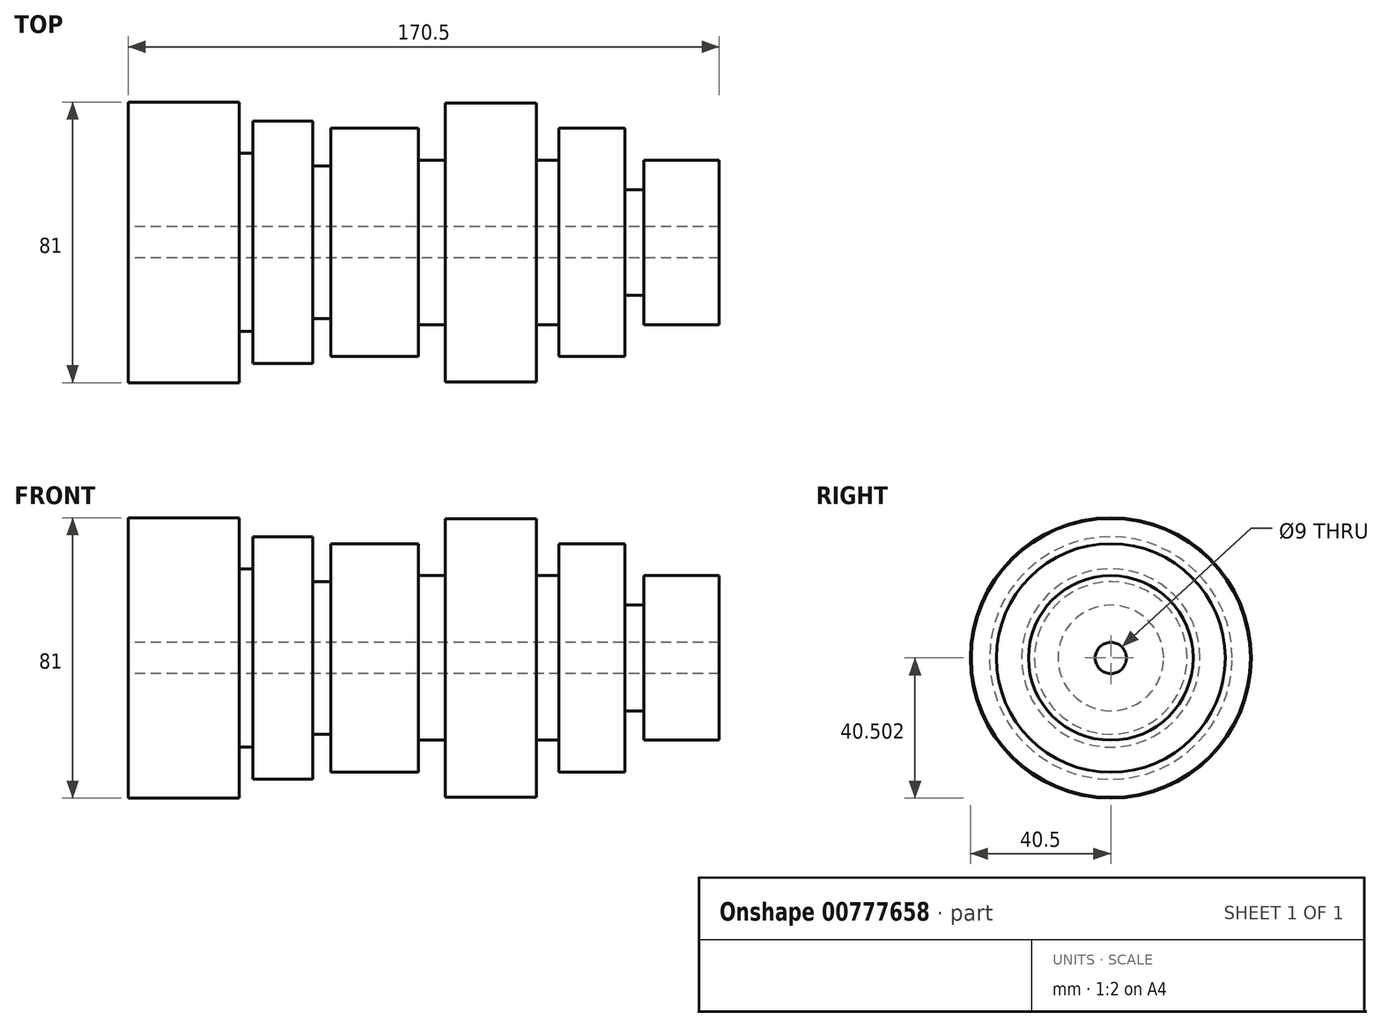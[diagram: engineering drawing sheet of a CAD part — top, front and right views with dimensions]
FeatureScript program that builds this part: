
annotation { "Feature Type Name" : "Feature", "Feature Type Description" : "" }
export const myFeature = defineFeature(function(context is Context, id is Id, definition is map)
    precondition{}
    {
        {
            var Q0;
            Q0=qCreatedBy(makeId("Front.planeOp"),FACE);
            var sketch = newSketch(context, id + "F0", { "sketchPlane" : qUnion([Q0])});
            skLineSegment(sketch, "E0", {"start": v(-87.13, -47.13) * mm, "end": v(83.37, -47.13) * mm});
            skLineSegment(sketch, "E1", {"start": v(-87.13, -47.13) * mm, "end": v(-87.13, -11.13) * mm});
            skLineSegment(sketch, "E2", {"start": v(-87.13, -11.13) * mm, "end": v(-55.13, -11.13) * mm});
            skLineSegment(sketch, "E3", {"start": v(-55.13, -11.13) * mm, "end": v(-55.13, -25.88) * mm});
            skLineSegment(sketch, "E4", {"start": v(-55.13, -25.88) * mm, "end": v(-51.13, -25.88) * mm});
            skLineSegment(sketch, "E5", {"start": v(-51.13, -25.88) * mm, "end": v(-51.13, -16.63) * mm});
            skLineSegment(sketch, "E6", {"start": v(-51.13, -16.63) * mm, "end": v(-33.88, -16.63) * mm});
            skLineSegment(sketch, "E7", {"start": v(-33.88, -16.63) * mm, "end": v(-33.88, -29.63) * mm});
            skLineSegment(sketch, "E8", {"start": v(83.37, -47.13) * mm, "end": v(83.37, -27.88) * mm});
            skLineSegment(sketch, "E9", {"start": v(83.37, -27.88) * mm, "end": v(61.63, -27.88) * mm});
            skLineSegment(sketch, "E10", {"start": v(61.63, -27.88) * mm, "end": v(61.63, -36.38) * mm});
            skLineSegment(sketch, "E11", {"start": v(61.63, -36.38) * mm, "end": v(56.13, -36.38) * mm});
            skLineSegment(sketch, "E12", {"start": v(56.13, -36.38) * mm, "end": v(56.13, -18.63) * mm});
            skLineSegment(sketch, "E13", {"start": v(56.13, -18.63) * mm, "end": v(37.12, -18.63) * mm});
            skLineSegment(sketch, "E14", {"start": v(37.12, -18.63) * mm, "end": v(37.12, -27.88) * mm});
            skLineSegment(sketch, "E15", {"start": v(37.12, -27.88) * mm, "end": v(30.62, -27.88) * mm});
            skLineSegment(sketch, "E16", {"start": v(30.62, -27.88) * mm, "end": v(30.62, -11.38) * mm});
            skLineSegment(sketch, "E17", {"start": v(30.62, -11.38) * mm, "end": v(4.37, -11.38) * mm});
            skLineSegment(sketch, "E18", {"start": v(4.37, -11.38) * mm, "end": v(4.37, -27.88) * mm});
            skLineSegment(sketch, "E19", {"start": v(-33.88, -29.63) * mm, "end": v(-28.63, -29.63) * mm});
            skLineSegment(sketch, "E20", {"start": v(-28.63, -29.63) * mm, "end": v(-28.63, -18.63) * mm});
            skLineSegment(sketch, "E21", {"start": v(-28.63, -18.63) * mm, "end": v(-3.38, -18.63) * mm});
            skLineSegment(sketch, "E22", {"start": v(-3.38, -18.63) * mm, "end": v(-3.38, -27.88) * mm});
            skLineSegment(sketch, "E23", {"start": v(-3.38, -27.88) * mm, "end": v(4.37, -27.88) * mm});
            skLineSegment(sketch, "E24", {"start": v(-88.38, -51.63) * mm, "end": v(83.37, -51.63) * mm});
            skSolve(sketch);
        }
        {
            var Q0;
            Q0=makeQuery(id+"F0.imprint","IMPRINT",FACE,{"disambiguationData":[TD([[makeQuery(id+"F0.imprint","IMPRINT",EDGE,{"derivedFrom":sQuery(id+"F0.wireOp",EDGE,"E0")}),1.0]])]});
            var Q1;
            Q1=sQuery(id+"F0.wireOp",EDGE,"E24");
            revolve(context, id + "F1", {"surfaceOperationType" : NewSurfaceOperationType.NEW, "entities" : qUnion([Q0]), "axis" : qUnion([Q1]), "revolveType" : RevolveType.FULL});
        }
    });
